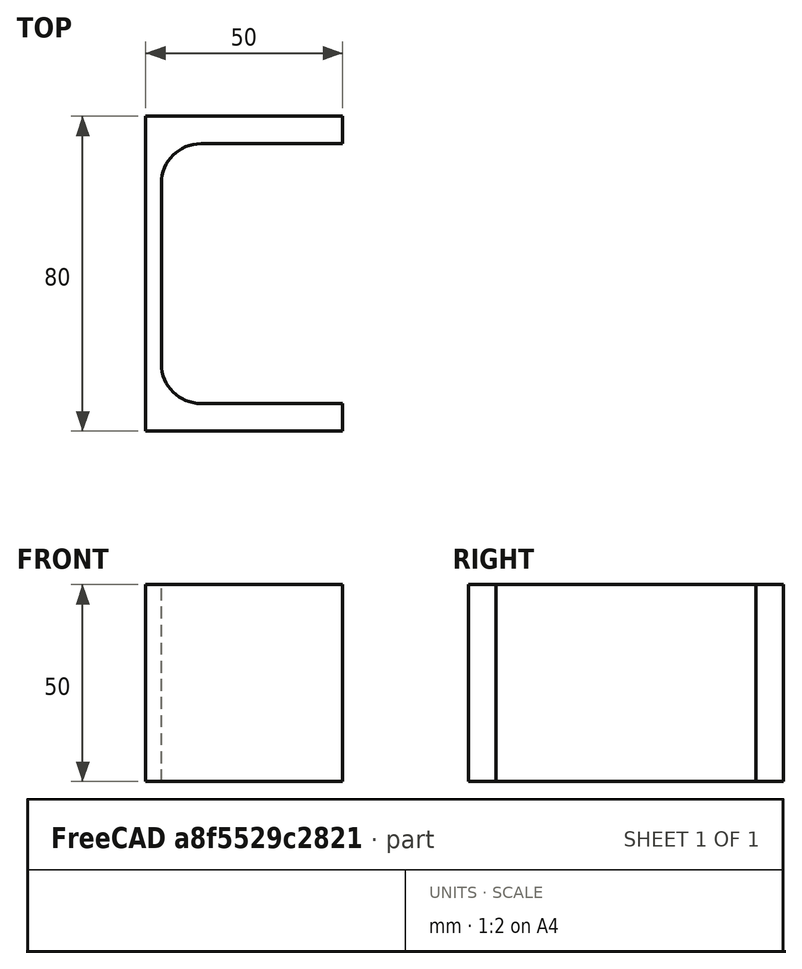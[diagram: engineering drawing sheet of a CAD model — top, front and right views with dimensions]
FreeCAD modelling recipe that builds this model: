
FCSTD DOCUMENT  (FreeCAD 0.20R29410 (Git))
Label: UPE-Profile 80 DIN1026-2 S235JR
License: All rights reserved
LicenseURL: http://en.wikipedia.org/wiki/All_rights_reserved
objects: Sketcher::SketchObject×1, Part::Extrusion×1
note: 2 computed .brp shape members not serialized (recipe doc carries the construction recipe); baked Part::Feature solids carry a one-line shape summary decoded from their .brp

FEATURE [Sketcher::SketchObject] Sketch
  FullyConstrained = true
  MapMode = 5
  sketch-geometry (10):
    g0: LineSegment StartX=4 StartY=-23 StartZ=0 EndX=4 EndY=23 EndZ=0
    g1: LineSegment StartX=14 StartY=33 StartZ=0 EndX=50 EndY=33 EndZ=0
    g2: LineSegment StartX=50 StartY=33 StartZ=0 EndX=50 EndY=40 EndZ=0
    g3: LineSegment StartX=50 StartY=-40 StartZ=0 EndX=50 EndY=-33 EndZ=0
    g4: LineSegment StartX=50 StartY=-33 StartZ=0 EndX=14 EndY=-33 EndZ=0
    g5: ArcOfCircle CenterX=14 CenterY=23 CenterZ=0 NormalX=0 NormalY=0 NormalZ=1 AngleXU=0 Radius=10 StartAngle=1.5708 EndAngle=3.14159
    g6: ArcOfCircle CenterX=14 CenterY=-23 CenterZ=0 NormalX=0 NormalY=0 NormalZ=1 AngleXU=0 Radius=10 StartAngle=3.14159 EndAngle=4.71239
    g7: LineSegment StartX=50 StartY=-40 StartZ=0 EndX=0 EndY=-40 EndZ=0
    g8: LineSegment StartX=0 StartY=-40 StartZ=0 EndX=0 EndY=40 EndZ=0
    g9: LineSegment StartX=0 StartY=40 StartZ=0 EndX=50 EndY=40 EndZ=0
  constraints (27):
    c: Vertical(g0)
    c: Coincident(g2,g1)
    c: Vertical(g2)
    c: Vertical(g3)
    c: Coincident(g4,g3)
    c: Horizontal(g4)
    c: Tangent(g1,g5) = 1.5708
    c: Tangent(g0,g5) = 1.5708
    c: Tangent(g0,g6) = 1.5708
    c: Tangent(g4,g6) = 1.5708
    c: Symmetric(g2,g3,g-1)
    c: DistanceY(g2) = 7
    c: Radius(g5) = 10
    c: Coincident(g3,g7)
    c: PointOnObject(g7,g-2)
    c: Horizontal(g7)
    c: Coincident(g7,g8)
    c: PointOnObject(g8,g-2)
    c: Coincident(g8,g9)
    c: Coincident(g9,g2)
    c: Horizontal(g9)
    c: Distance(g-1,g0) = 4
    c: DistanceX(g9,g9) = 50
    c: Horizontal(g1)
    c: Equal(g3,g2)
    c: Equal(g5,g6)
    c: DistanceY(g3,g2) = 80
FEATURE [Part::Extrusion] Extrude  label="UPE-Profile 80 DIN1026-2 S235JR"
  Base = -> Sketch
  Dir = (0,0,50)
  DirMode = 0
  FaceMakerClass = Part::FaceMakerExtrusion
  LengthFwd = 0
  LengthRev = 0
  Solid = true
  Symmetric = false
